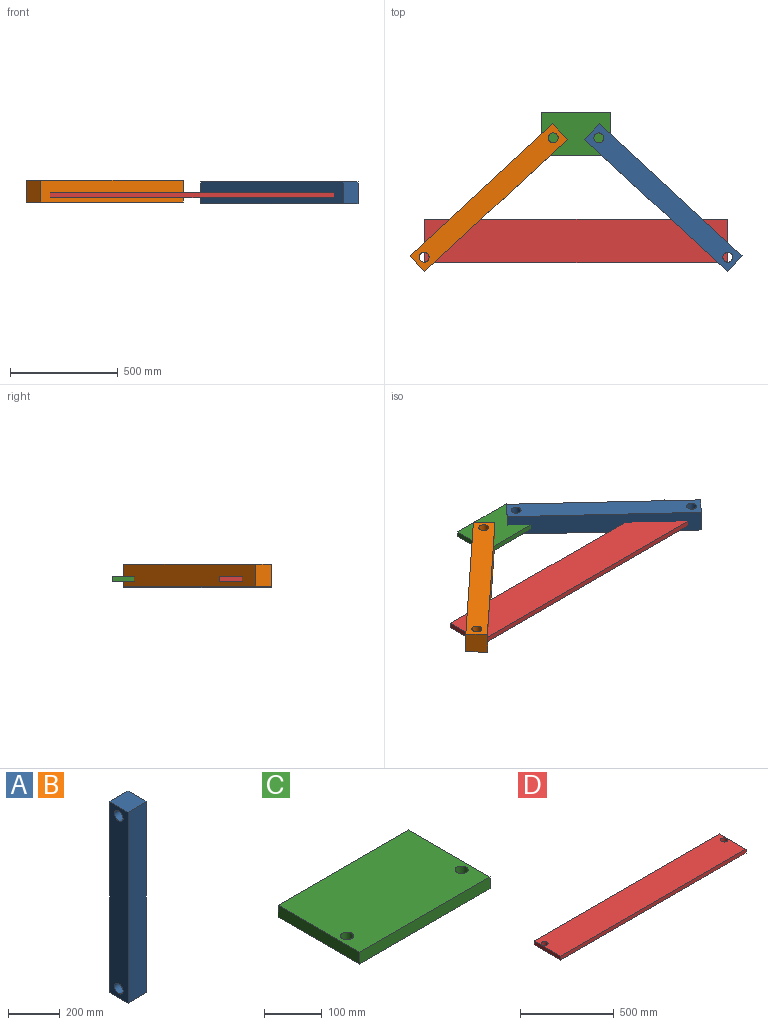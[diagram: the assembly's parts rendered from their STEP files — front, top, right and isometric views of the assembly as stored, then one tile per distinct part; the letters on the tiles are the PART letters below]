
ASSEMBLY  parts=4 mates=5
PART A: 8 faces, bbox 100x100x900 mm
  f0: plane 900x100mm, normal (1,0,0), area 86672.3mm2, adj f2,f3,f4,f5,f6,f7
  f1: plane 900x100mm, normal (-1,0,0), area 86672.3mm2, adj f2,f3,f4,f5,f6,f7
  f2: plane 900x100mm, normal (0,-1,0), area 90000mm2, adj f0,f1,f4,f5
  f3: plane 900x100mm, normal (0,1,0), area 90000mm2, adj f0,f1,f4,f5
  f4: plane 100x100mm, normal (0,0,1), area 10000mm2, adj f0,f1,f2,f3
  f5: plane 100x100mm, normal (0,0,-1), area 10000mm2, adj f0,f1,f2,f3
  f6: cylinder r=23.01mm len=100mm, axis (-1,0,0), area 14459.8mm2, adj f0,f1
  f7: cylinder r=23.01mm len=100mm, axis (-1,0,0), area 14459.8mm2, adj f0,f1
PART B: same geometry as A
PART C: 8 faces, bbox 320x200x25 mm
  f0: plane 320x200mm, normal (0,0,1), area 63195.3mm2, adj f2,f3,f4,f5,f6,f7
  f1: plane 320x200mm, normal (0,0,-1), area 63195.3mm2, adj f2,f3,f4,f5,f6,f7
  f2: plane 320x25mm, normal (0,1,0), area 8000mm2, adj f0,f1,f3,f5
  f3: plane 200x25mm, normal (-1,0,0), area 5000mm2, adj f0,f1,f2,f4
  f4: plane 320x25mm, normal (0,-1,0), area 8000mm2, adj f0,f1,f3,f5
  f5: plane 200x25mm, normal (1,0,0), area 5000mm2, adj f0,f1,f2,f4
  f6: cylinder r=11.32mm len=25mm, axis (0,0,1), area 1777.7mm2, adj f0,f1
  f7: cylinder r=11.32mm len=25mm, axis (0,0,1), area 1777.7mm2, adj f0,f1
PART D: 8 faces, bbox 1400x200x25 mm
  f0: plane 1400x200mm, normal (0,0,1), area 277775.6mm2, adj f2,f3,f4,f5,f6,f7
  f1: plane 1400x200mm, normal (0,0,-1), area 277775.6mm2, adj f2,f3,f4,f5,f6,f7
  f2: plane 1400x25mm, normal (0,1,0), area 35000mm2, adj f0,f1,f3,f5
  f3: plane 200x25mm, normal (-1,0,0), area 5000mm2, adj f0,f1,f2,f4
  f4: plane 1400x25mm, normal (0,-1,0), area 35000mm2, adj f0,f1,f3,f5
  f5: plane 200x25mm, normal (1,0,0), area 5000mm2, adj f0,f1,f2,f4
  f6: cylinder r=18.82mm len=37.63mm, axis (0,0,1), area 2955.5mm2, adj f0,f1
  f7: cylinder r=18.82mm len=37.63mm, axis (0,0,1), area 2955.5mm2, adj f0,f1
PLACE A rot(axis=(-0.34,-0.87,-0.34),97.6deg) t=(115.76,-445.73,23.83)mm
PLACE B rot(axis=(-0.68,-0.27,-0.68),150.1deg) t=(-1354.16,-445.73,31.17)mm
PLACE C t=(-219.66,-56.97,0)mm fixed
PLACE D rot(axis=(0,0,-1),180deg) t=(291.35,130.07,0)mm
MATE cylindrical A.f1 <-> C.f6  axis (0,0,-1) through (-478.7,103.73,-26.17)mm
MATE cylindrical D.f1 <-> A.f0  axis (0,0,-1) through (49.3,-384.3,0)mm
MATE cylindrical B.f0 <-> D.f1  axis (0,0,1) through (-1287.7,-384.3,81.17)mm
MATE cylindrical B.f1 <-> C.f7  axis (0,0,-1) through (-759.7,103.73,-18.83)mm
MATE parallel C.f2 <-> D.f2  axis (0,1,0) through (-619.2,253.73,12.5)mm
